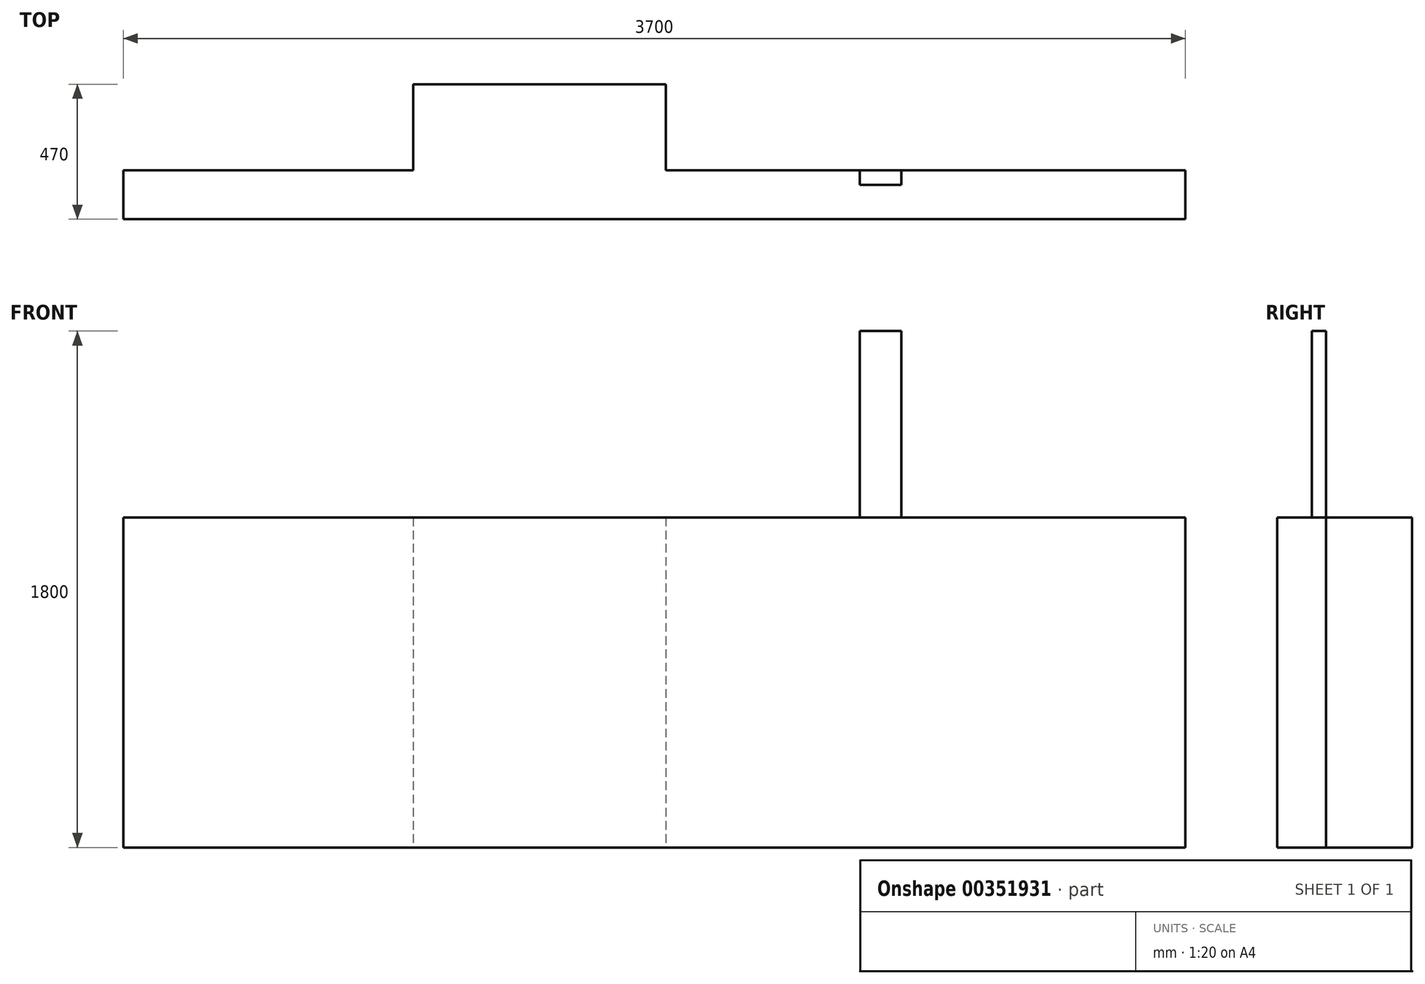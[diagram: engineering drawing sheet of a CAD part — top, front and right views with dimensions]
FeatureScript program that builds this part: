
annotation { "Feature Type Name" : "Feature", "Feature Type Description" : "" }
export const myFeature = defineFeature(function(context is Context, id is Id, definition is map)
    precondition{}
    {
        {
            var Q0;
            Q0=qCreatedBy(makeId("Top.planeOp"),FACE);
            var sketch = newSketch(context, id + "F0", { "sketchPlane" : qUnion([Q0])});
            skLineSegment(sketch, "E0", {"start": v(-1948.1, 395.85) * mm, "end": v(-1948.1, -1174.15) * mm});
            skLineSegment(sketch, "E1", {"start": v(-1948.1, -1174.15) * mm, "end": v(-138.1, -1174.15) * mm});
            skLineSegment(sketch, "E2", {"start": v(-138.1, -1174.15) * mm, "end": v(701.9, -1174.15) * mm});
            skLineSegment(sketch, "E3", {"start": v(701.9, -1174.15) * mm, "end": v(1751.9, -1174.15) * mm});
            skLineSegment(sketch, "E4", {"start": v(1751.9, -1174.15) * mm, "end": v(1751.9, 225.85) * mm});
            skLineSegment(sketch, "E5", {"start": v(1751.9, 225.85) * mm, "end": v(1751.9, 395.85) * mm});
            skLineSegment(sketch, "E6", {"start": v(1751.9, 395.85) * mm, "end": v(616.9, 395.85) * mm});
            skLineSegment(sketch, "E7", {"start": v(761.9, 395.85) * mm, "end": v(616.9, 395.85) * mm});
            skLineSegment(sketch, "E8", {"start": v(-58.1, 395.85) * mm, "end": v(-58.1, 695.85) * mm});
            skLineSegment(sketch, "E9", {"start": v(-58.1, 695.85) * mm, "end": v(-938.1, 695.85) * mm});
            skLineSegment(sketch, "E10", {"start": v(-938.1, 695.85) * mm, "end": v(-938.1, 395.85) * mm});
            skLineSegment(sketch, "E11", {"start": v(-938.1, 395.85) * mm, "end": v(-1948.1, 395.85) * mm});
            skLineSegment(sketch, "E12", {"start": v(1751.9, 225.85) * mm, "end": v(-1948.1, 225.85) * mm});
            skLineSegment(sketch, "E13", {"start": v(616.9, 395.85) * mm, "end": v(616.9, 345.85) * mm});
            skLineSegment(sketch, "E14", {"start": v(616.9, 345.85) * mm, "end": v(761.9, 345.85) * mm});
            skLineSegment(sketch, "E15", {"start": v(761.9, 345.85) * mm, "end": v(761.9, 395.85) * mm});
            skLineSegment(sketch, "E16", {"start": v(616.9, 395.85) * mm, "end": v(-58.1, 395.85) * mm});
            skSolve(sketch);
        }
        {
            var Q0;
            Q0=makeQuery(id+"F0.imprint","IMPRINT",FACE,{"disambiguationData":[TD([[makeQuery(id+"F0.imprint","IMPRINT",EDGE,{"derivedFrom":sQuery(id+"F0.wireOp",EDGE,"E5")}),1.0]])]});
            extrude(context, id + "F1", {"entities" : qUnion([Q0]), "depth" : 1150 * mm});
        }
        {
            var Q0;
            {var subQ2=sQuery(id+"F0.wireOp",EDGE,"E13");Q0=makeQuery(id+"F0.imprint","IMPRINT",FACE,{"disambiguationData":[TD([[makeQuery(id+"F0.imprint","IMPRINT",EDGE,{"derivedFrom":subQ2}),1.0]])]});}
            extrude(context, id + "F2", {"entities" : qUnion([Q0]), "operationType" : NewBodyOperationType.ADD, "depth" : 1800 * mm});
        }
        {
            var Q0;
            Q0=sQuery(id+"F0.wireOp",EDGE,"E11");
            var Q1;
            Q1=sQuery(id+"F0.wireOp",EDGE,"E10");
            var Q2;
            Q2=sQuery(id+"F0.wireOp",EDGE,"E8");
            var Q3;
            Q3=sQuery(id+"F0.wireOp",EDGE,"E6");
            var Q4;
            Q4=sQuery(id+"F0.wireOp",EDGE,"E4");
            var Q5;
            Q5=sQuery(id+"F0.wireOp",EDGE,"E5");
            var Q6;
            Q6=sQuery(id+"F0.wireOp",EDGE,"E16");
            extrude(context, id + "F3", {"bodyType" : ToolBodyType.SURFACE, "surfaceEntities" : qUnion([Q0, Q1, Q2, Q3, Q4, Q5, Q6]), "depth" : 2000 * mm});
        }
        {
            var Q0;
            Q0=sQuery(id+"F0.wireOp",EDGE,"E0");
            var Q1;
            Q1=sQuery(id+"F0.wireOp",EDGE,"E1");
            var Q2;
            Q2=sQuery(id+"F0.wireOp",EDGE,"E3");
            extrude(context, id + "F4", {"bodyType" : ToolBodyType.SURFACE, "surfaceEntities" : qUnion([Q0, Q1, Q2]), "depth" : 500 * mm});
        }
    });
